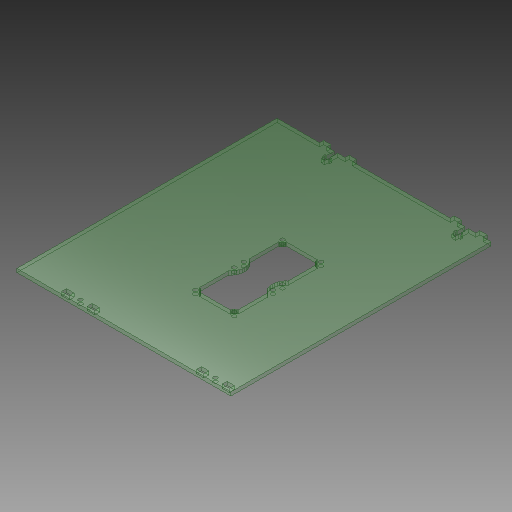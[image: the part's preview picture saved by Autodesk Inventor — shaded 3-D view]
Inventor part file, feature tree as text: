
AUTODESK INVENTOR PART (.ipt)
format: ipt  version: 2018 (Build 220112000, 112)  size: 783,872 bytes
history: native  units: mm
features: extrude x1, hole x1, sketch x1, projected_geometry x1
ambient origin geometry x8: Origin, YZ Plane, XZ Plane, XY Plane, X Axis, Y Axis, Z Axis, Center Point
bodies: Solid1 (feature_tree)
feature tree (4):
  extrude  "Extrusion1"  [1 undecoded]
  hole  "Hole1"  [1 undecoded]
  sketch  "Sketch2"  dims[d0=3.0mm d1=0.0mm d2=3.4mm d3=6.0mm d4=4.0mm d5=2.0mm d6=90.0deg d7=8.0mm d8=20.594885mm]
  projected_geometry  "Projected Loop1"
note: 2 required parameter values undecoded (feature->parameter linkage not recoverable at this tier; creation-order binding heuristic only, values carry confidence <= 0.55)
